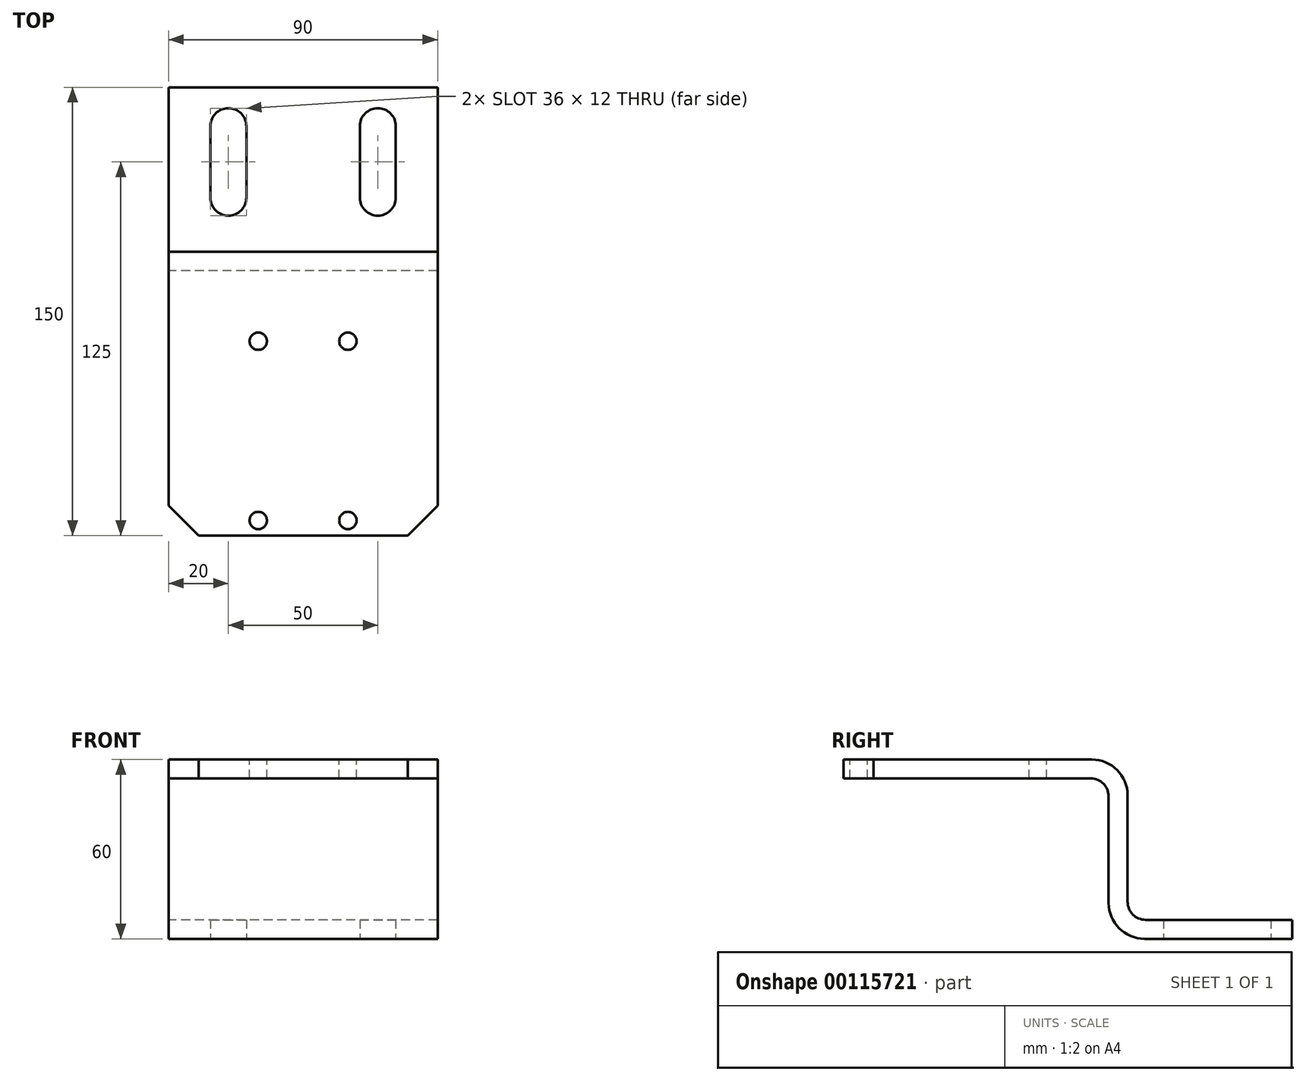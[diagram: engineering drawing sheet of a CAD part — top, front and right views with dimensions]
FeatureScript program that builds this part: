
annotation { "Feature Type Name" : "Feature", "Feature Type Description" : "" }
export const myFeature = defineFeature(function(context is Context, id is Id, definition is map)
    precondition{}
    {
        {
            var Q0;
            Q0=qCreatedBy(makeId("Right.planeOp"),FACE);
            var sketch = newSketch(context, id + "F0", { "sketchPlane" : qUnion([Q0])});
            skLineSegment(sketch, "E0", {"start": v(0, 0) * mm, "end": v(83, 0) * mm});
            skLineSegment(sketch, "E1", {"start": v(95, -12) * mm, "end": v(95, -47.65) * mm});
            skLineSegment(sketch, "E2", {"start": v(101, -53.65) * mm, "end": v(150, -53.65) * mm});
            skLineSegment(sketch, "E3.0", {"start": v(100.65, -60) * mm, "end": v(150, -60) * mm});
            skLineSegment(sketch, "E3.1", {"start": v(88.65, -12.35) * mm, "end": v(88.65, -48) * mm});
            skLineSegment(sketch, "E3.2", {"start": v(0, -6.35) * mm, "end": v(82.65, -6.35) * mm});
            skLineSegment(sketch, "E4", {"start": v(0, 0) * mm, "end": v(0, -6.35) * mm});
            skLineSegment(sketch, "E5", {"start": v(150, -53.65) * mm, "end": v(150, -60) * mm});
            skPoint(sketch, "E6.visualSharp", {"position": v(88.65, -6.35) * mm});
            skArc(sketch, "E6.filletArc", {"start": v(88.65, -12.35) * mm, "mid": v(86.9, -8.1) * mm, "end": v(82.65, -6.35) * mm});
            skPoint(sketch, "E7.visualSharp", {"position": v(95, -53.65) * mm});
            skArc(sketch, "E7.filletArc", {"start": v(95, -47.65) * mm, "mid": v(96.76, -51.9) * mm, "end": v(101, -53.65) * mm});
            skPoint(sketch, "E8.visualSharp", {"position": v(95, 0) * mm});
            skArc(sketch, "E8.filletArc", {"start": v(95, -12) * mm, "mid": v(91.49, -3.51) * mm, "end": v(83, 0) * mm});
            skPoint(sketch, "E9.visualSharp", {"position": v(88.65, -60) * mm});
            skArc(sketch, "E9.filletArc", {"start": v(88.65, -48) * mm, "mid": v(92.16, -56.49) * mm, "end": v(100.65, -60) * mm});
            skSolve(sketch);
        }
        {
            var Q0;
            Q0 = qSketchRegion(id + "F0", true);
            extrude(context, id + "F1", {"entities" : qUnion([Q0]), "endBound" : BoundingType.SYMMETRIC, "depth" : 90 * mm});
        }
        {
            var Q0;
            Q0=makeQuery(id+"F1.opExtrude","CAP_EDGE",EDGE,{"disambiguationData":[OSD([sQuery(id+"F0.wireOp",EDGE,"E4")])],"isStart":false});
            var Q1;
            Q1=makeQuery(id+"F1.opExtrude","CAP_EDGE",EDGE,{"disambiguationData":[OSD([sQuery(id+"F0.wireOp",EDGE,"E4")])],"isStart":true});
            chamfer(context, id + "F2", {"entities" : qUnion([Q0, Q1]), "width" : 10 * mm, "tangentPropagation" : true});
        }
        {
            var Q0;
            Q0=makeQuery(id+"F1.opExtrude","SWEPT_FACE",FACE,{"disambiguationData":[OSD([sQuery(id+"F0.wireOp",EDGE,"E0")])]});
            var sketch = newSketch(context, id + "F3", { "sketchPlane" : qUnion([Q0])});
            skLineSegment(sketch, "E10.0", {"start": v(35, 0) * mm, "end": v(-35, 0) * mm, "construction": true});
            skLineSegment(sketch, "E11.0", {"start": v(35, 5) * mm, "end": v(-35, 5) * mm, "construction": true});
            skLineSegment(sketch, "E12.0", {"start": v(35, 65) * mm, "end": v(-35, 65) * mm, "construction": true});
            skLineSegment(sketch, "E13", {"start": v(0, 65) * mm, "end": v(0, 5) * mm, "construction": true});
            skLineSegment(sketch, "E14.0", {"start": v(-15, 65) * mm, "end": v(-15, 5) * mm, "construction": true});
            skLineSegment(sketch, "E15.MirrorCS", {"start": v(15, 65) * mm, "end": v(15, 5) * mm, "construction": true});
            skPoint(sketch, "E16", {"position": v(-15, 5) * mm});
            skPoint(sketch, "E17", {"position": v(-15, 65) * mm});
            skPoint(sketch, "E18", {"position": v(15, 5) * mm});
            skPoint(sketch, "E19", {"position": v(15, 65) * mm});
            skSolve(sketch);
        }
        {
            var Q0;
            Q0=sQuery(id+"F3.wireOp",VERTEX,"E16");
            var Q1;
            Q1=sQuery(id+"F3.wireOp",VERTEX,"E17");
            var Q2;
            Q2=sQuery(id+"F3.wireOp",VERTEX,"E19");
            var Q3;
            Q3=sQuery(id+"F3.wireOp",VERTEX,"E18");
            var Q4;
            Q4=makeQuery(id+"F1.opExtrude","SWEPT_BODY",BODY,{"disambiguationData":[OSD([sQuery(id+"F0.wireOp",EDGE,"E0"),sQuery(id+"F0.wireOp",EDGE,"E1"),sQuery(id+"F0.wireOp",EDGE,"E2"),sQuery(id+"F0.wireOp",EDGE,"E3.0"),sQuery(id+"F0.wireOp",EDGE,"E3.1"),sQuery(id+"F0.wireOp",EDGE,"E3.2"),sQuery(id+"F0.wireOp",EDGE,"E4"),sQuery(id+"F0.wireOp",EDGE,"E5"),sQuery(id+"F0.wireOp",EDGE,"E6.filletArc"),sQuery(id+"F0.wireOp",EDGE,"E7.filletArc"),sQuery(id+"F0.wireOp",EDGE,"E8.filletArc"),sQuery(id+"F0.wireOp",EDGE,"E9.filletArc")])]});
            hole(context, id + "F4", {"style" : HoleStyle.SIMPLE, "endStyle" : HoleEndStyle.THROUGH, "standardTappedOrClearance" : lookupTablePath({ "standard" : "ISO", "size" : "5.8", "type" : "Drilled" }), "standardBlindInLast" : lookupTablePath({ "standard" : "ISO", "size" : "5.8", "type" : "Drilled" }), "holeDiameter" : 5.8 * mm, "locations" : qUnion([Q0, Q1, Q2, Q3]), "scope" : qUnion([Q4]), "isTappedThrough" : true});
        }
        {
            var Q0;
            Q0=makeQuery(id+"F1.opExtrude","SWEPT_FACE",FACE,{"disambiguationData":[OSD([sQuery(id+"F0.wireOp",EDGE,"E3.0")])]});
            var sketch = newSketch(context, id + "F5", { "sketchPlane" : qUnion([Q0])});
            skLineSegment(sketch, "E20.0", {"start": v(45, -150) * mm, "end": v(-45, -150) * mm, "construction": true});
            skLineSegment(sketch, "E21", {"start": v(0, -150) * mm, "end": v(0, -100.65) * mm, "construction": true});
            skLineSegment(sketch, "E22.0", {"start": v(45, -125) * mm, "end": v(-45, -125) * mm, "construction": true});
            skLineSegment(sketch, "E23.0", {"start": v(45, -137) * mm, "end": v(-45, -137) * mm, "construction": true});
            skLineSegment(sketch, "E24", {"start": v(25, -137) * mm, "end": v(25, -125) * mm});
            skLineSegment(sketch, "E25.MirrorCS", {"start": v(25, -113) * mm, "end": v(25, -125) * mm});
            skArc(sketch, "E26.0.startCap", {"start": v(19, -113) * mm, "mid": v(25, -107) * mm, "end": v(31, -113) * mm});
            skLineSegment(sketch, "E26.0.left", {"start": v(31, -113) * mm, "end": v(31, -125) * mm});
            skLineSegment(sketch, "E26.0.right", {"start": v(19, -113) * mm, "end": v(19, -125) * mm});
            skArc(sketch, "E26.1.startCap", {"start": v(31, -137) * mm, "mid": v(25, -143) * mm, "end": v(19, -137) * mm});
            skLineSegment(sketch, "E26.1.left", {"start": v(19, -137) * mm, "end": v(19, -125) * mm});
            skLineSegment(sketch, "E26.1.right", {"start": v(31, -137) * mm, "end": v(31, -125) * mm});
            skLineSegment(sketch, "E27.MirrorCS", {"start": v(-31, -137) * mm, "end": v(-31, -125) * mm});
            skLineSegment(sketch, "E28.MirrorCS", {"start": v(-31, -113) * mm, "end": v(-31, -125) * mm});
            skLineSegment(sketch, "E29.MirrorCS", {"start": v(-25, -137) * mm, "end": v(-25, -125) * mm});
            skLineSegment(sketch, "E30.MirrorCS", {"start": v(-25, -113) * mm, "end": v(-25, -125) * mm});
            skLineSegment(sketch, "E31.MirrorCS", {"start": v(-19, -137) * mm, "end": v(-19, -125) * mm});
            skArc(sketch, "E32.MirrorCS", {"start": v(-31, -137) * mm, "mid": v(-25, -143) * mm, "end": v(-19, -137) * mm});
            skLineSegment(sketch, "E33.MirrorCS", {"start": v(-19, -113) * mm, "end": v(-19, -125) * mm});
            skArc(sketch, "E34.MirrorCS", {"start": v(-19, -113) * mm, "mid": v(-25, -107) * mm, "end": v(-31, -113) * mm});
            skSolve(sketch);
        }
        {
            var Q0;
            Q0 = qSketchRegion(id + "F5", true);
            extrude(context, id + "F6", {"entities" : qUnion([Q0]), "operationType" : NewBodyOperationType.REMOVE, "endBound" : BoundingType.THROUGH_ALL, "oppositeDirection" : true, "depth" : 25 * mm});
        }
    });
